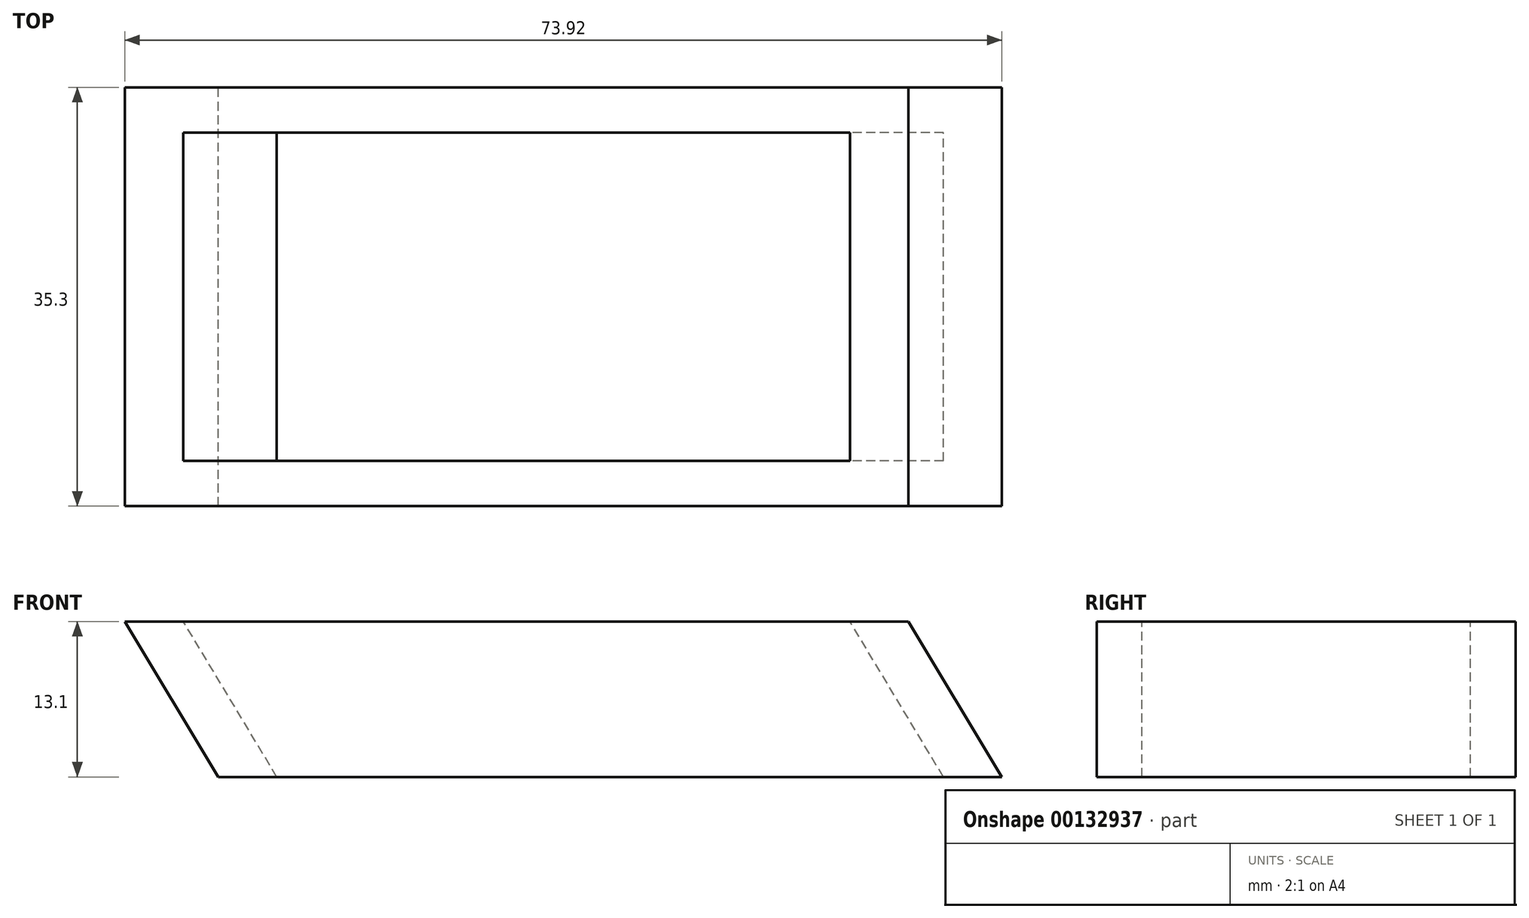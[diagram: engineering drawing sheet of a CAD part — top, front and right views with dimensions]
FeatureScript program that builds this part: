
annotation { "Feature Type Name" : "Feature", "Feature Type Description" : "" }
export const myFeature = defineFeature(function(context is Context, id is Id, definition is map)
    precondition{}
    {
        {
            var Q0;
            Q0=qCreatedBy(makeId("Top.planeOp"),FACE);
            var sketch = newSketch(context, id + "F0", { "sketchPlane" : qUnion([Q0])});
            skLineSegment(sketch, "E0.bottom", {"start": v(33.02, -17.65) * mm, "end": v(-33.02, -17.65) * mm});
            skLineSegment(sketch, "E0.top", {"start": v(33.02, 17.65) * mm, "end": v(-33.02, 17.65) * mm});
            skLineSegment(sketch, "E0.left", {"start": v(33.02, -17.65) * mm, "end": v(33.02, 17.65) * mm});
            skLineSegment(sketch, "E0.right", {"start": v(-33.02, -17.65) * mm, "end": v(-33.02, 17.65) * mm});
            skPoint(sketch, "E0.middle", {"position": v(0, 0) * mm});
            skLineSegment(sketch, "E1.bottom", {"start": v(28.1, -13.86) * mm, "end": v(-28.1, -13.86) * mm});
            skLineSegment(sketch, "E1.top", {"start": v(28.1, 13.86) * mm, "end": v(-28.1, 13.86) * mm});
            skLineSegment(sketch, "E1.left", {"start": v(28.1, -13.86) * mm, "end": v(28.1, 13.86) * mm});
            skLineSegment(sketch, "E1.right", {"start": v(-28.1, -13.86) * mm, "end": v(-28.1, 13.86) * mm});
            skSolve(sketch);
        }
        {
            var Q0;
            Q0=qCreatedBy(makeId("Front.planeOp"),FACE);
            var sketch = newSketch(context, id + "F1", { "sketchPlane" : qUnion([Q0])});
            skLineSegment(sketch, "E2", {"start": v(0, 0) * mm, "end": v(-7.88, 13.1) * mm});
            skSolve(sketch);
        }
        {
            var Q0;
            Q0=makeQuery(id+"F0.imprint","IMPRINT",FACE,{"disambiguationData":[TD([[makeQuery(id+"F0.imprint","IMPRINT",EDGE,{"derivedFrom":sQuery(id+"F0.wireOp",EDGE,"E0.bottom")}),-1.0]])]});
            var Q1;
            Q1=sQuery(id+"F1.wireOp",EDGE,"E2");
            sweep(context, id + "F2", {"profiles" : qUnion([Q0]), "path" : qUnion([Q1])});
        }
    });
